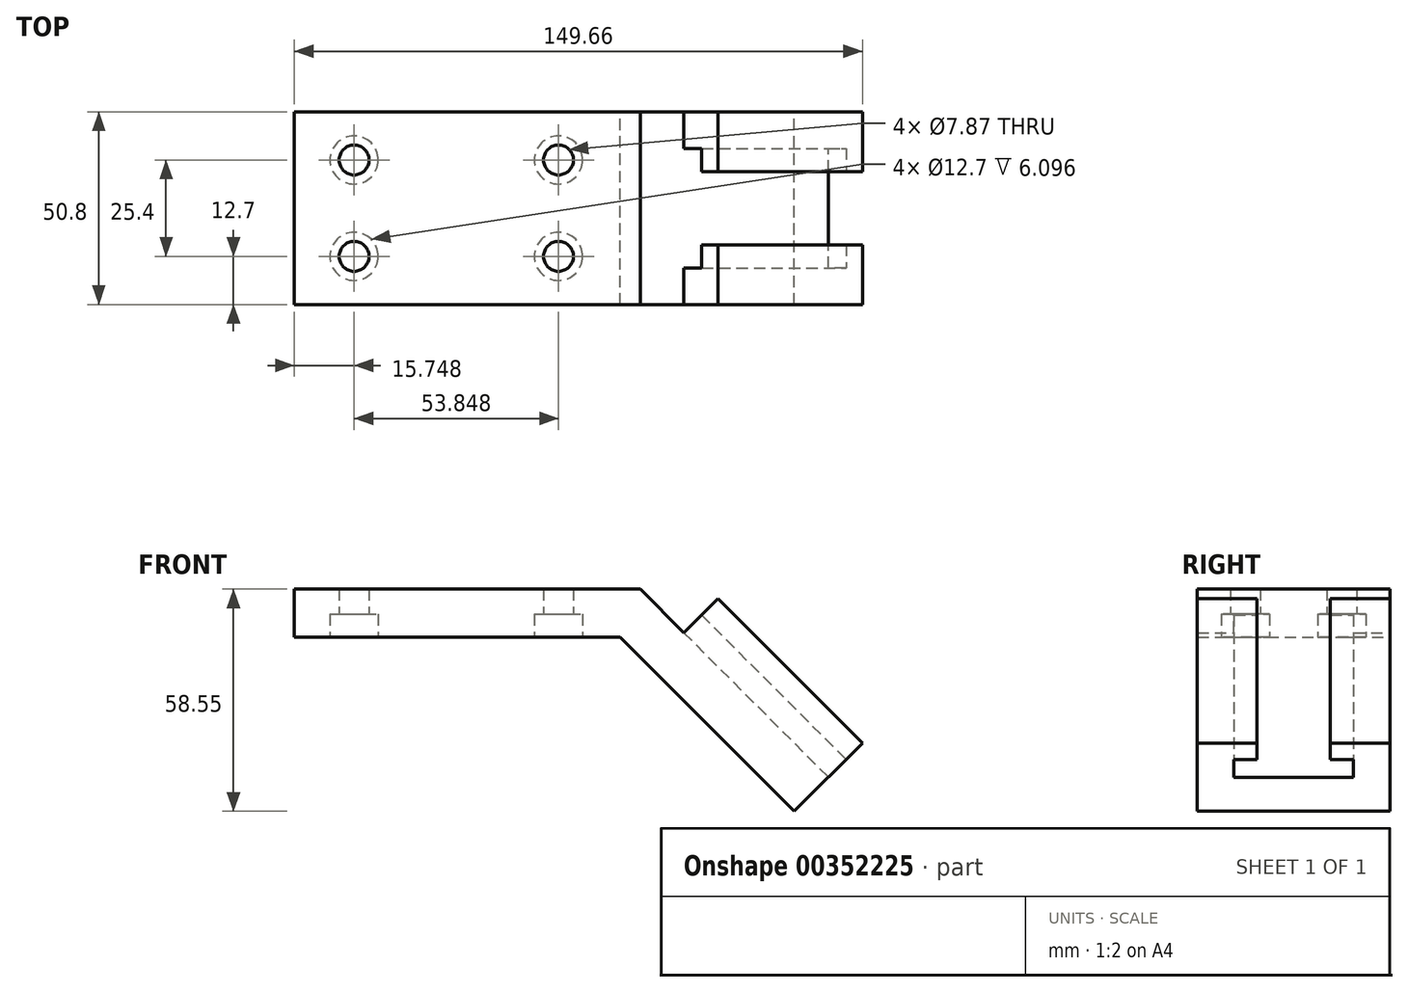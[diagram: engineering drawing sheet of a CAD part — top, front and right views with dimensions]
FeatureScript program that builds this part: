
annotation { "Feature Type Name" : "Feature", "Feature Type Description" : "" }
export const myFeature = defineFeature(function(context is Context, id is Id, definition is map)
    precondition{}
    {
        {
            var Q0;
            Q0=qCreatedBy(makeId("Front.planeOp"),FACE);
            var sketch = newSketch(context, id + "F0", { "sketchPlane" : qUnion([Q0])});
            skLineSegment(sketch, "E0", {"start": v(0, 0) * mm, "end": v(0, 12.7) * mm});
            skLineSegment(sketch, "E1", {"start": v(0, 12.7) * mm, "end": v(91.11, 12.7) * mm});
            skLineSegment(sketch, "E2", {"start": v(131.7, -45.85) * mm, "end": v(85.85, 0) * mm});
            skLineSegment(sketch, "E3", {"start": v(85.85, 0) * mm, "end": v(0, 0) * mm});
            skLineSegment(sketch, "E4", {"start": v(91.11, 12.7) * mm, "end": v(102.6, 1.2) * mm});
            skLineSegment(sketch, "E5", {"start": v(102.6, 1.2) * mm, "end": v(111.59, 10.19) * mm});
            skLineSegment(sketch, "E6", {"start": v(111.59, 10.19) * mm, "end": v(149.66, -27.9) * mm});
            skLineSegment(sketch, "E7", {"start": v(149.66, -27.9) * mm, "end": v(131.7, -45.85) * mm});
            skSolve(sketch);
        }
        {
            var Q0;
            Q0=makeQuery(id+"F0.imprint","IMPRINT",FACE,{"disambiguationData":[TD([[makeQuery(id+"F0.imprint","IMPRINT",EDGE,{"derivedFrom":sQuery(id+"F0.wireOp",EDGE,"E0")}),-1.0]])]});
            extrude(context, id + "F1", {"entities" : qUnion([Q0]), "depth" : 50.8 * mm});
        }
        {
            var Q0;
            Q0=makeQuery(id+"F1.opExtrude","SWEPT_FACE",FACE,{"disambiguationData":[OSD([sQuery(id+"F0.wireOp",EDGE,"E7")])]});
            var sketch = newSketch(context, id + "F2", { "sketchPlane" : qUnion([Q0])});
            skLineSegment(sketch, "E8", {"start": v(-35.05, 86.1) * mm, "end": v(-35.05, 80.01) * mm});
            skLineSegment(sketch, "E9", {"start": v(-35.05, 80.01) * mm, "end": v(-41.15, 80.01) * mm});
            skLineSegment(sketch, "E10", {"start": v(-41.15, 80.01) * mm, "end": v(-41.15, 73.4) * mm});
            skLineSegment(sketch, "E11", {"start": v(-41.15, 73.4) * mm, "end": v(-9.65, 73.4) * mm});
            skLineSegment(sketch, "E12", {"start": v(-9.65, 73.4) * mm, "end": v(-9.65, 80.01) * mm});
            skLineSegment(sketch, "E13", {"start": v(-9.65, 80.01) * mm, "end": v(-15.75, 80.01) * mm});
            skLineSegment(sketch, "E14", {"start": v(-15.75, 80.01) * mm, "end": v(-15.75, 86.1) * mm});
            skLineSegment(sketch, "E15", {"start": v(-35.05, 86.1) * mm, "end": v(-15.75, 86.1) * mm});
            skSolve(sketch);
        }
        {
            var Q0;
            Q0=makeQuery(id+"F2.imprint","IMPRINT",FACE,{"disambiguationData":[TD([[makeQuery(id+"F2.imprint","IMPRINT",EDGE,{"derivedFrom":sQuery(id+"F2.wireOp",EDGE,"E8")}),1.0]])]});
            extrude(context, id + "F3", {"entities" : qUnion([Q0]), "operationType" : NewBodyOperationType.REMOVE, "endBound" : BoundingType.THROUGH_ALL, "oppositeDirection" : true, "depth" : 25.4 * mm});
        }
        {
            var Q0;
            {var subQ1=sQuery(id+"F0.wireOp",EDGE,"E6");Q0=makeQuery(id+"F3.boolean.opBoolean","SPLIT",FACE,{"disambiguationData":[TD([makeQuery(id+"F3.opExtrude","SWEPT_FACE",FACE,{"disambiguationData":[OSD([sQuery(id+"F2.wireOp",EDGE,"E8")])]})])],"derivedFrom":makeQuery(id+"F1.opExtrude","SWEPT_FACE",FACE,{"disambiguationData":[OSD([subQ1])]})});}
            var sketch = newSketch(context, id + "F4", { "sketchPlane" : qUnion([Q0])});
            skArc(sketch, "E16", {"start": v(71.7, 28.45) * mm, "mid": v(125.55, -25.4) * mm, "end": v(71.7, -79.25) * mm});
            skLineSegment(sketch, "E17", {"start": v(119.18, -50.8) * mm, "end": v(125.55, -50.8) * mm});
            skLineSegment(sketch, "E18", {"start": v(125.55, -50.8) * mm, "end": v(125.55, -25.4) * mm});
            skLineSegment(sketch, "E19", {"start": v(125.55, -25.4) * mm, "end": v(125.55, 0) * mm});
            skLineSegment(sketch, "E20", {"start": v(125.55, 0) * mm, "end": v(119.18, 0) * mm});
            skSolve(sketch);
        }
        {
            var Q0;
            {var subQ0=sQuery(id+"F4.wireOp",EDGE,"E19");Q0=makeQuery(id+"F4.imprint","IMPRINT",FACE,{"disambiguationData":[TD([[makeQuery(id+"F4.imprint","IMPRINT",EDGE,{"derivedFrom":subQ0}),1.0]])]});}
            var Q1;
            {var subQ0=sQuery(id+"F4.wireOp",EDGE,"E17");Q1=makeQuery(id+"F4.imprint","IMPRINT",FACE,{"disambiguationData":[TD([[makeQuery(id+"F4.imprint","IMPRINT",EDGE,{"derivedFrom":subQ0}),1.0]])]});}
            var Q2;
            {var subQ0=sQuery(id+"F4.wireOp",EDGE,"E18");var subQ1=sQuery(id+"F4.wireOp",EDGE,"E16");var subQ2=makeQuery(id+"F4.imprint","INTERSECT",VERTEX,{"derivedFrom":[subQ1,subQ0,sQuery(id+"F4.wireOp",EDGE,"E19")]});Q2=makeQuery(id+"F4.imprint","IMPRINT",FACE,{"disambiguationData":[TD([[makeQuery(id+"F4.imprint","IMPRINT",EDGE,{"disambiguationData":[TD([[subQ2,-1.0]])],"derivedFrom":subQ1}),1.0]])]});}
            extrude(context, id + "F5", {"entities" : qUnion([Q0, Q1, Q2]), "operationType" : NewBodyOperationType.REMOVE, "oppositeDirection" : true, "depth" : 25.4 * mm});
        }
        {
            var Q0;
            Q0=makeQuery(id+"F1.opExtrude","SWEPT_FACE",FACE,{"disambiguationData":[OSD([sQuery(id+"F0.wireOp",EDGE,"E3")])]});
            var sketch = newSketch(context, id + "F6", { "sketchPlane" : qUnion([Q0])});
            skPoint(sketch, "E21", {"position": v(15.75, 38.1) * mm});
            skPoint(sketch, "E22", {"position": v(69.6, 38.1) * mm});
            skPoint(sketch, "E23", {"position": v(69.6, 12.7) * mm});
            skPoint(sketch, "E24", {"position": v(15.75, 12.7) * mm});
            skSolve(sketch);
        }
        {
            var Q0;
            Q0=sQuery(id+"F6.wireOp",VERTEX,"E21");
            var Q1;
            Q1=sQuery(id+"F6.wireOp",VERTEX,"E24");
            var Q2;
            Q2=sQuery(id+"F6.wireOp",VERTEX,"E23");
            var Q3;
            Q3=sQuery(id+"F6.wireOp",VERTEX,"E22");
            var Q4;
            Q4=makeQuery(id+"F1.opExtrude","SWEPT_BODY",BODY,{"disambiguationData":[OSD([sQuery(id+"F0.wireOp",EDGE,"E0"),sQuery(id+"F0.wireOp",EDGE,"E1"),sQuery(id+"F0.wireOp",EDGE,"E2"),sQuery(id+"F0.wireOp",EDGE,"E3"),sQuery(id+"F0.wireOp",EDGE,"E4"),sQuery(id+"F0.wireOp",EDGE,"E5"),sQuery(id+"F0.wireOp",EDGE,"E6"),sQuery(id+"F0.wireOp",EDGE,"E7")])]});
            hole(context, id + "F7", {"style" : HoleStyle.C_BORE, "endStyle" : HoleEndStyle.BLIND, "holeDiameter" : 7.87 * mm, "cBoreDiameter" : 12.7 * mm, "cBoreDepth" : 6.1 * mm, "holeDepth" : 50.8 * mm, "isTappedThrough" : true, "tappedDepth" : 12.7 * mm, "tapClearance" : 3, "locations" : qUnion([Q0, Q1, Q2, Q3]), "scope" : qUnion([Q4])});
        }
    });
